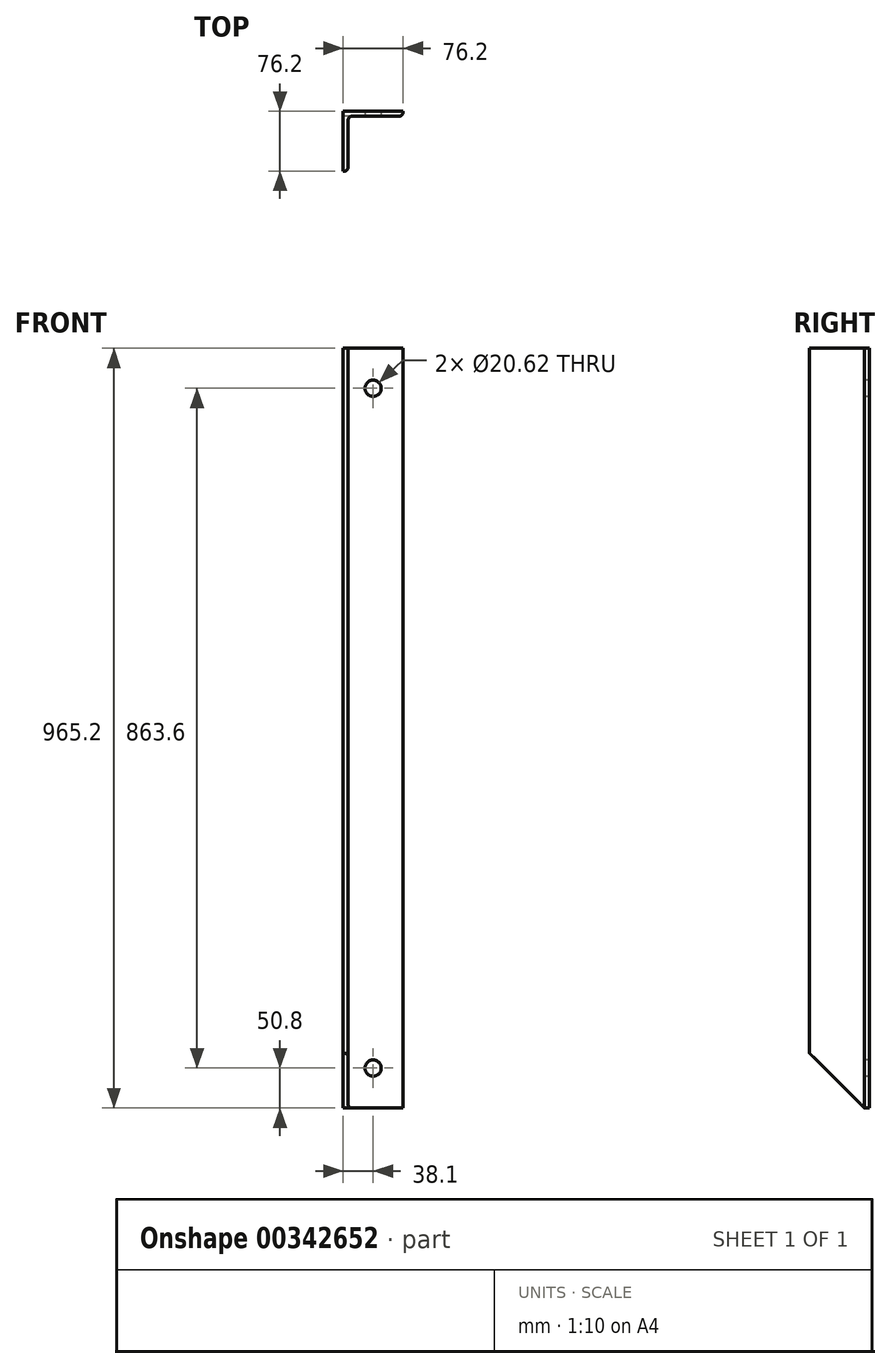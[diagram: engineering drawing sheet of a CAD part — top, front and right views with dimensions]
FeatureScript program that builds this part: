
annotation { "Feature Type Name" : "Feature", "Feature Type Description" : "" }
export const myFeature = defineFeature(function(context is Context, id is Id, definition is map)
    precondition{}
    {
        {
            var Q0;
            Q0=qCreatedBy(makeId("Top.planeOp"),FACE);
            var sketch = newSketch(context, id + "F0", { "sketchPlane" : qUnion([Q0])});
            skLineSegment(sketch, "E0", {"start": v(0, 0) * mm, "end": v(0, 76.2) * mm});
            skLineSegment(sketch, "E1", {"start": v(0, 76.2) * mm, "end": v(76.2, 76.2) * mm});
            skLineSegment(sketch, "E2", {"start": v(76.2, 76.2) * mm, "end": v(76.2, 69.85) * mm});
            skLineSegment(sketch, "E3", {"start": v(76.2, 69.85) * mm, "end": v(6.35, 69.85) * mm});
            skLineSegment(sketch, "E4", {"start": v(6.35, 69.85) * mm, "end": v(6.35, 0) * mm});
            skLineSegment(sketch, "E5", {"start": v(6.35, 0) * mm, "end": v(0, 0) * mm});
            skSolve(sketch);
        }
        {
            var Q0;
            Q0 = qSketchRegion(id + "F0", true);
            extrude(context, id + "F1", {"entities" : qUnion([Q0]), "endBound" : BoundingType.SYMMETRIC, "depth" : 965.2 * mm});
        }
        {
            var Q0;
            Q0=qCreatedBy(makeId("Right.planeOp"),FACE);
            var sketch = newSketch(context, id + "F2", { "sketchPlane" : qUnion([Q0])});
            skPoint(sketch, "E6.0", {"position": v(69.85, -482.6) * mm});
            skLineSegment(sketch, "E7", {"start": v(69.85, -482.6) * mm, "end": v(0, -412.75) * mm});
            skSolve(sketch);
        }
        {
            var Q0;
            Q0=makeQuery(id+"F1.opExtrude","SWEPT_FACE",FACE,{"disambiguationData":[OSD([sQuery(id+"F0.wireOp",EDGE,"E0")])]});
            var sketch = newSketch(context, id + "F3", { "sketchPlane" : qUnion([Q0])});
            skPoint(sketch, "E8.0", {"position": v(-69.85, -482.6) * mm});
            skPoint(sketch, "E9.0", {"position": v(0, -412.75) * mm});
            skLineSegment(sketch, "E10", {"start": v(0, -412.75) * mm, "end": v(0, -482.6) * mm});
            skLineSegment(sketch, "E11", {"start": v(0, -482.6) * mm, "end": v(-69.85, -482.6) * mm});
            skSolve(sketch);
        }
        {
            var Q0;
            {var subQ4=sQuery(id+"F3.wireOp",EDGE,"E10");Q0=makeQuery(id+"F3.imprint","IMPRINT",FACE,{"disambiguationData":[TD([[makeQuery(id+"F3.imprint","IMPRINT",EDGE,{"derivedFrom":subQ4}),-1.0]])]});}
            var sketch = newSketch(context, id + "F4", { "sketchPlane" : qUnion([Q0])});
            skPoint(sketch, "E12.0", {"position": v(-69.85, -482.6) * mm});
            skPoint(sketch, "E13.0", {"position": v(0, -412.75) * mm});
            skPoint(sketch, "E14.0", {"position": v(0, -482.6) * mm});
            skLineSegment(sketch, "E15", {"start": v(-69.85, -482.6) * mm, "end": v(0, -412.75) * mm});
            skLineSegment(sketch, "E16", {"start": v(0, -482.6) * mm, "end": v(-69.85, -482.6) * mm});
            skSolve(sketch);
        }
        {
            var Q0;
            Q0=makeQuery(id+"F4.imprint","IMPRINT",FACE,{"disambiguationData":[TD([[makeQuery(id+"F4.imprint","IMPRINT",EDGE,{"derivedFrom":sQuery(id+"F4.wireOp",EDGE,"E15")}),-1.0]])]});
            extrude(context, id + "F5", {"entities" : qUnion([Q0]), "operationType" : NewBodyOperationType.REMOVE, "oppositeDirection" : true, "depth" : 6.35 * mm});
        }
        {
            var Q0;
            Q0=qCreatedBy(makeId("Front.planeOp"),FACE);
            var sketch = newSketch(context, id + "F6", { "sketchPlane" : qUnion([Q0])});
            skCircle(sketch, "E17", {"center": v(38.1, 431.8) * mm, "radius": 10.31 * mm});
            skCircle(sketch, "E18", {"center": v(38.1, -431.8) * mm, "radius": 10.31 * mm});
            skSolve(sketch);
        }
        {
            var Q0;
            Q0=makeQuery(id+"F6.imprint","IMPRINT",FACE,{"disambiguationData":[TD([[makeQuery(id+"F6.imprint","IMPRINT",EDGE,{"derivedFrom":sQuery(id+"F6.wireOp",EDGE,"E17")}),1.0]])]});
            var Q1;
            Q1=makeQuery(id+"F6.imprint","IMPRINT",FACE,{"disambiguationData":[TD([[makeQuery(id+"F6.imprint","IMPRINT",EDGE,{"derivedFrom":sQuery(id+"F6.wireOp",EDGE,"E18")}),1.0]])]});
            extrude(context, id + "F7", {"entities" : qUnion([Q0, Q1]), "operationType" : NewBodyOperationType.REMOVE, "oppositeDirection" : true, "depth" : 76.2 * mm});
        }
        {
            var Q0;
            Q0=makeQuery(id+"F1.opExtrude","SWEPT_EDGE",EDGE,{"disambiguationData":[OSD([sQuery(id+"F0.wireOp",EDGE,"E3"),sQuery(id+"F0.wireOp",EDGE,"E4")])]});
            var Q1;
            Q1=makeQuery(id+"F1.opExtrude","SWEPT_EDGE",EDGE,{"disambiguationData":[OSD([sQuery(id+"F0.wireOp",EDGE,"E2"),sQuery(id+"F0.wireOp",EDGE,"E3")])]});
            var Q2;
            Q2=makeQuery(id+"F1.opExtrude","SWEPT_EDGE",EDGE,{"disambiguationData":[OSD([sQuery(id+"F0.wireOp",EDGE,"E4"),sQuery(id+"F0.wireOp",EDGE,"E5")])]});
            fillet(context, id + "F8", {"entities" : qUnion([Q0, Q1, Q2]), "radius" : 5.08 * mm, "tangentPropagation" : true, "allowEdgeOverflow" : false});
        }
    });
